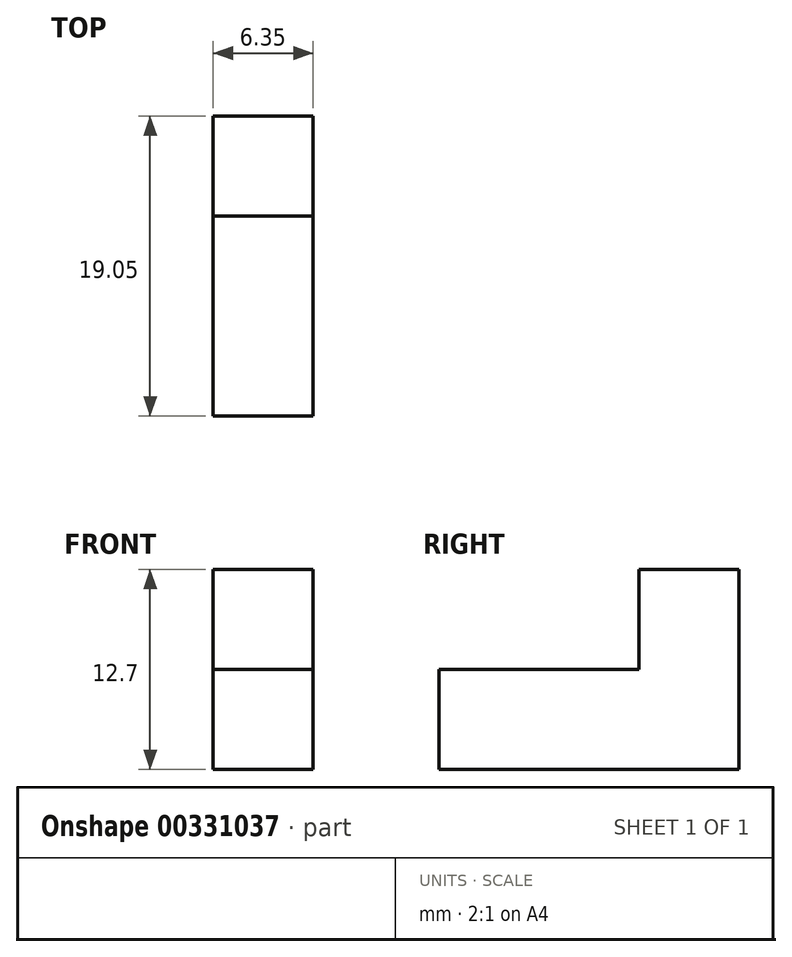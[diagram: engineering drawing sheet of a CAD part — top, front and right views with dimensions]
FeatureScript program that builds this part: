
annotation { "Feature Type Name" : "Feature", "Feature Type Description" : "" }
export const myFeature = defineFeature(function(context is Context, id is Id, definition is map)
    precondition{}
    {
        {
            var Q0;
            Q0=qCreatedBy(makeId("Top.planeOp"),FACE);
            var sketch = newSketch(context, id + "F0", { "sketchPlane" : qUnion([Q0])});
            skLineSegment(sketch, "E0.bottom", {"start": v(8.4, 22.47) * mm, "end": v(14.76, 22.47) * mm});
            skLineSegment(sketch, "E0.top", {"start": v(8.4, 3.42) * mm, "end": v(14.76, 3.42) * mm});
            skLineSegment(sketch, "E0.left", {"start": v(8.4, 22.47) * mm, "end": v(8.4, 3.42) * mm});
            skLineSegment(sketch, "E0.right", {"start": v(14.76, 22.47) * mm, "end": v(14.76, 3.42) * mm});
            skLineSegment(sketch, "E1", {"start": v(14.76, 22.47) * mm, "end": v(14.76, 16.12) * mm, "construction": true});
            skLineSegment(sketch, "E2", {"start": v(14.76, 16.12) * mm, "end": v(8.4, 16.12) * mm});
            skSolve(sketch);
        }
        {
            var Q0;
            {var subQ0=sQuery(id+"F0.wireOp",EDGE,"E0.bottom");Q0=makeQuery(id+"F0.imprint","IMPRINT",FACE,{"disambiguationData":[TD([[makeQuery(id+"F0.imprint","IMPRINT",EDGE,{"derivedFrom":subQ0}),-1.0]])]});}
            extrude(context, id + "F1", {"entities" : qUnion([Q0]), "depth" : 12.7 * mm});
        }
        {
            var Q0;
            {var subQ0=sQuery(id+"F0.wireOp",EDGE,"E0.top");Q0=makeQuery(id+"F0.imprint","IMPRINT",FACE,{"disambiguationData":[TD([[makeQuery(id+"F0.imprint","IMPRINT",EDGE,{"derivedFrom":subQ0}),1.0]])]});}
            extrude(context, id + "F2", {"entities" : qUnion([Q0]), "operationType" : NewBodyOperationType.ADD, "depth" : 6.35 * mm});
        }
    });
